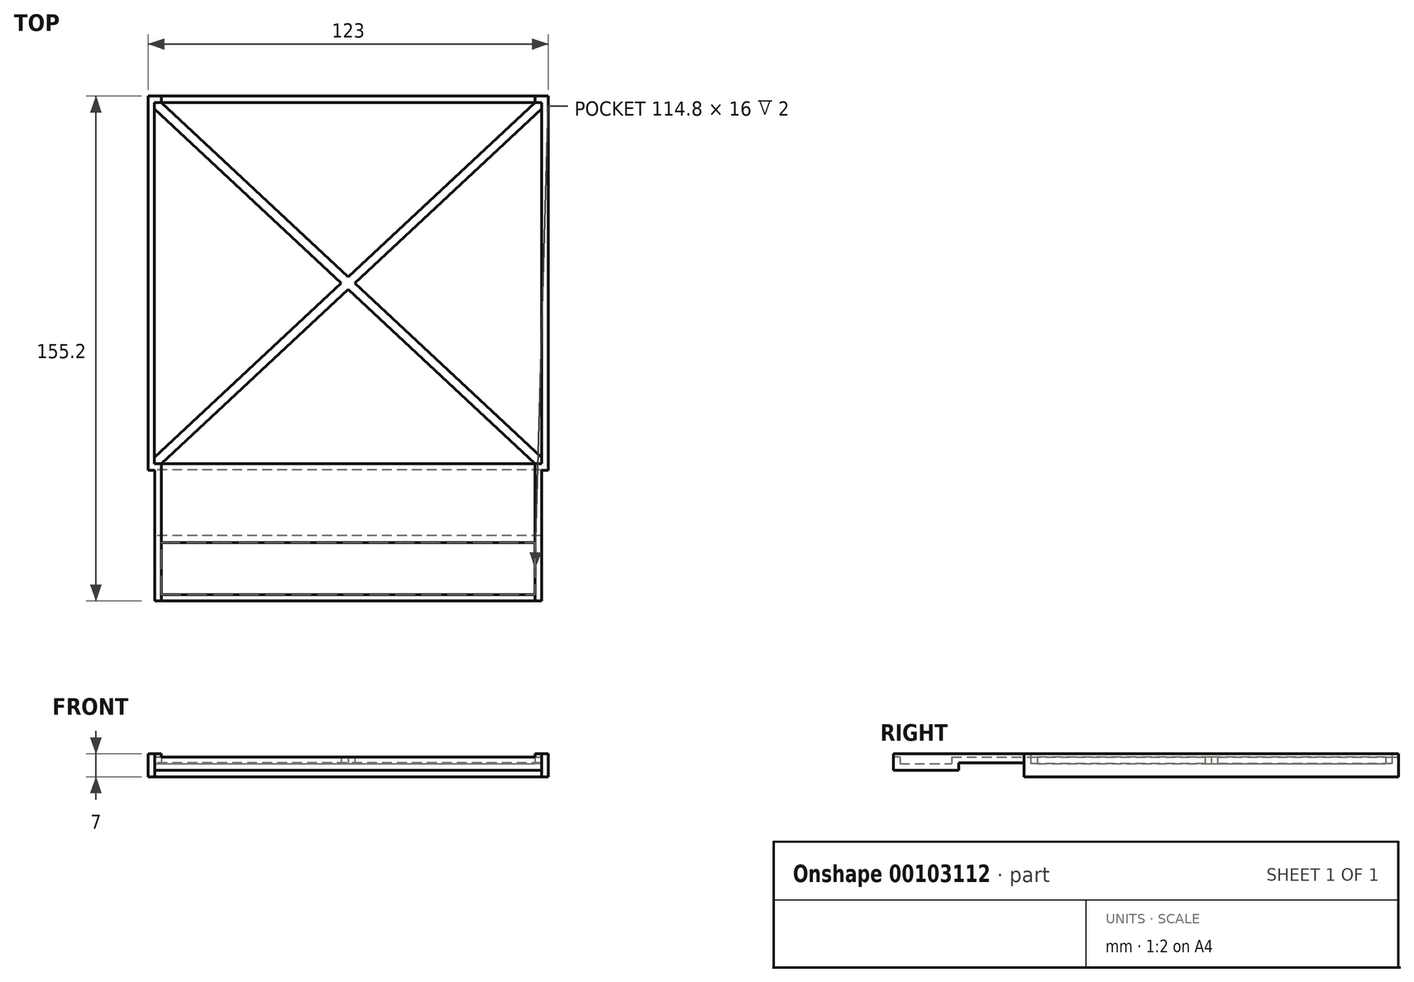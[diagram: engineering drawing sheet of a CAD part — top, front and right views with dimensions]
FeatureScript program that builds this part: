
annotation { "Feature Type Name" : "Feature", "Feature Type Description" : "" }
export const myFeature = defineFeature(function(context is Context, id is Id, definition is map)
    precondition{}
    {
        {
            var Q0;
            Q0=qCreatedBy(makeId("Top.planeOp"),FACE);
            var sketch = newSketch(context, id + "F0", { "sketchPlane" : qUnion([Q0])});
            skLineSegment(sketch, "E0.bottom", {"start": v(0, 0) * mm, "end": v(118.8, 0) * mm});
            skLineSegment(sketch, "E0.left", {"start": v(0, 0) * mm, "end": v(0, 40.2) * mm});
            skLineSegment(sketch, "E0.right", {"start": v(118.8, 0) * mm, "end": v(118.8, 40.2) * mm});
            skLineSegment(sketch, "E1.bottom", {"start": v(-2.1, 40.2) * mm, "end": v(0, 40.2) * mm});
            skLineSegment(sketch, "E1.top", {"start": v(-2.1, 155.2) * mm, "end": v(120.9, 155.2) * mm});
            skLineSegment(sketch, "E1.left", {"start": v(-2.1, 40.2) * mm, "end": v(-2.1, 155.2) * mm});
            skLineSegment(sketch, "E1.right", {"start": v(120.9, 40.2) * mm, "end": v(120.9, 155.2) * mm});
            skLineSegment(sketch, "E2.trimOffspring", {"start": v(118.8, 40.2) * mm, "end": v(120.9, 40.2) * mm});
            skSolve(sketch);
        }
        {
            var Q0;
            Q0=makeQuery(id+"F0.imprint","IMPRINT",FACE,{"disambiguationData":[TD([[makeQuery(id+"F0.imprint","IMPRINT",EDGE,{"derivedFrom":sQuery(id+"F0.wireOp",EDGE,"E0.bottom")}),1.0]])]});
            extrude(context, id + "F1", {"entities" : qUnion([Q0]), "depth" : 2 * mm});
        }
        {
            var Q0;
            Q0=makeQuery(id+"F1.opExtrude","CAP_FACE",FACE,{"disambiguationData":[OSD([sQuery(id+"F0.wireOp",EDGE,"E0.bottom"),sQuery(id+"F0.wireOp",EDGE,"E0.left"),sQuery(id+"F0.wireOp",EDGE,"E0.right"),sQuery(id+"F0.wireOp",EDGE,"E1.bottom"),sQuery(id+"F0.wireOp",EDGE,"E1.top"),sQuery(id+"F0.wireOp",EDGE,"E1.left"),sQuery(id+"F0.wireOp",EDGE,"E1.right"),sQuery(id+"F0.wireOp",EDGE,"E2.trimOffspring")])],"isStart":false});
            var sketch = newSketch(context, id + "F2", { "sketchPlane" : qUnion([Q0])});
            skLineSegment(sketch, "E3.0", {"start": v(-0.1, 42.2) * mm, "end": v(2, 42.2) * mm});
            skLineSegment(sketch, "E3.1", {"start": v(2, 2) * mm, "end": v(2, 42.2) * mm});
            skLineSegment(sketch, "E3.2", {"start": v(-0.1, 42.2) * mm, "end": v(-0.1, 153.2) * mm});
            skLineSegment(sketch, "E3.3", {"start": v(2, 2) * mm, "end": v(116.8, 2) * mm});
            skLineSegment(sketch, "E3.4", {"start": v(-0.1, 153.2) * mm, "end": v(118.9, 153.2) * mm});
            skLineSegment(sketch, "E3.5", {"start": v(118.9, 42.2) * mm, "end": v(118.9, 153.2) * mm});
            skLineSegment(sketch, "E3.6", {"start": v(116.8, 42.2) * mm, "end": v(118.9, 42.2) * mm});
            skLineSegment(sketch, "E3.7", {"start": v(116.8, 2) * mm, "end": v(116.8, 42.2) * mm});
            skSolve(sketch);
        }
        {
            var Q0;
            Q0=makeQuery(id+"F2.imprint","IMPRINT",FACE,{"disambiguationData":[TD([[makeQuery(id+"F2.imprint","IMPRINT",EDGE,{"derivedFrom":sQuery(id+"F2.wireOp",EDGE,"E3.0")}),-1.0]])]});
            extrude(context, id + "F3", {"entities" : qUnion([Q0]), "operationType" : NewBodyOperationType.ADD, "depth" : 3 * mm});
        }
        {
            var Q0;
            Q0=makeQuery(id+"F1.opExtrude","CAP_FACE",FACE,{"disambiguationData":[OSD([sQuery(id+"F0.wireOp",EDGE,"E0.bottom"),sQuery(id+"F0.wireOp",EDGE,"E0.left"),sQuery(id+"F0.wireOp",EDGE,"E0.right"),sQuery(id+"F0.wireOp",EDGE,"E1.bottom"),sQuery(id+"F0.wireOp",EDGE,"E1.top"),sQuery(id+"F0.wireOp",EDGE,"E1.left"),sQuery(id+"F0.wireOp",EDGE,"E1.right"),sQuery(id+"F0.wireOp",EDGE,"E2.trimOffspring")])],"isStart":false});
            var sketch = newSketch(context, id + "F4", { "sketchPlane" : qUnion([Q0])});
            skLineSegment(sketch, "E4.bottom", {"start": v(2, 42.2) * mm, "end": v(116.8, 42.2) * mm});
            skLineSegment(sketch, "E4.top", {"start": v(2, 18) * mm, "end": v(116.8, 18) * mm});
            skLineSegment(sketch, "E4.left", {"start": v(2, 42.2) * mm, "end": v(2, 18) * mm});
            skLineSegment(sketch, "E4.right", {"start": v(116.8, 42.2) * mm, "end": v(116.8, 18) * mm});
            skLineSegment(sketch, "E5", {"start": v(-0.1, 42.2) * mm, "end": v(118.9, 153.2) * mm});
            skLineSegment(sketch, "E6", {"start": v(-0.1, 153.2) * mm, "end": v(118.9, 42.2) * mm});
            skLineSegment(sketch, "E7", {"start": v(-0.1, 44.16) * mm, "end": v(57.3, 97.7) * mm});
            skLineSegment(sketch, "E8", {"start": v(57.3, 97.7) * mm, "end": v(-0.1, 151.24) * mm});
            skLineSegment(sketch, "E9", {"start": v(2, 42.2) * mm, "end": v(59.4, 95.74) * mm});
            skLineSegment(sketch, "E10", {"start": v(59.4, 95.74) * mm, "end": v(116.8, 42.2) * mm});
            skLineSegment(sketch, "E11", {"start": v(2, 153.2) * mm, "end": v(59.4, 99.66) * mm});
            skLineSegment(sketch, "E12", {"start": v(59.4, 99.66) * mm, "end": v(116.8, 153.2) * mm});
            skLineSegment(sketch, "E13", {"start": v(118.9, 151.24) * mm, "end": v(61.5, 97.7) * mm});
            skLineSegment(sketch, "E14", {"start": v(61.5, 97.7) * mm, "end": v(118.9, 44.16) * mm});
            skSolve(sketch);
        }
        {
            var Q0;
            Q0=makeQuery(id+"F4.imprint","IMPRINT",FACE,{"disambiguationData":[TD([[makeQuery(id+"F4.imprint","IMPRINT",EDGE,{"derivedFrom":sQuery(id+"F4.wireOp",EDGE,"E4.bottom")}),-1.0]])]});
            var Q1;
            Q1=makeQuery(id+"F4.imprint","IMPRINT",FACE,{"disambiguationData":[TD([[makeQuery(id+"F4.imprint","IMPRINT",EDGE,{"derivedFrom":sQuery(id+"F4.wireOp",EDGE,"E9")}),1.0]])]});
            var Q2;
            {var subQ1=sQuery(id+"F4.wireOp",EDGE,"E13");Q2=makeQuery(id+"F4.imprint","IMPRINT",FACE,{"disambiguationData":[TD([[makeQuery(id+"F4.imprint","IMPRINT",EDGE,{"derivedFrom":subQ1}),-1.0]])]});}
            var Q3;
            {var subQ1=sQuery(id+"F4.wireOp",EDGE,"E11");Q3=makeQuery(id+"F4.imprint","IMPRINT",FACE,{"disambiguationData":[TD([[makeQuery(id+"F4.imprint","IMPRINT",EDGE,{"derivedFrom":subQ1}),-1.0]])]});}
            var Q4;
            {var subQ1=sQuery(id+"F4.wireOp",EDGE,"E7");Q4=makeQuery(id+"F4.imprint","IMPRINT",FACE,{"disambiguationData":[TD([[makeQuery(id+"F4.imprint","IMPRINT",EDGE,{"derivedFrom":subQ1}),-1.0]])]});}
            extrude(context, id + "F5", {"entities" : qUnion([Q0, Q1, Q2, Q3, Q4]), "operationType" : NewBodyOperationType.ADD, "depth" : 2 * mm});
        }
        {
            var Q0;
            Q0=makeQuery(id+"F1.opExtrude","CAP_FACE",FACE,{"disambiguationData":[OSD([sQuery(id+"F0.wireOp",EDGE,"E0.bottom"),sQuery(id+"F0.wireOp",EDGE,"E0.left"),sQuery(id+"F0.wireOp",EDGE,"E0.right"),sQuery(id+"F0.wireOp",EDGE,"E1.bottom"),sQuery(id+"F0.wireOp",EDGE,"E1.top"),sQuery(id+"F0.wireOp",EDGE,"E1.left"),sQuery(id+"F0.wireOp",EDGE,"E1.right"),sQuery(id+"F0.wireOp",EDGE,"E2.trimOffspring")])],"isStart":true});
            var sketch = newSketch(context, id + "F6", { "sketchPlane" : qUnion([Q0])});
            skLineSegment(sketch, "E15.bottom", {"start": v(118.8, -40.3) * mm, "end": v(0, -40.3) * mm});
            skLineSegment(sketch, "E15.top", {"start": v(118.8, -20.1) * mm, "end": v(0, -20.1) * mm});
            skLineSegment(sketch, "E15.left", {"start": v(118.8, -40.3) * mm, "end": v(118.8, -20.1) * mm});
            skLineSegment(sketch, "E15.right", {"start": v(0, -40.3) * mm, "end": v(0, -20.1) * mm});
            skSolve(sketch);
        }
        {
            var Q0;
            {var subQ5=sQuery(id+"F6.wireOp",EDGE,"E15.bottom");Q0=makeQuery(id+"F6.imprint","IMPRINT",FACE,{"disambiguationData":[TD([[makeQuery(id+"F6.imprint","IMPRINT",EDGE,{"derivedFrom":subQ5}),-1.0]])]});}
            extrude(context, id + "F7", {"entities" : qUnion([Q0]), "operationType" : NewBodyOperationType.REMOVE, "oppositeDirection" : true, "depth" : 2.2 * mm});
        }
        {
            var Q0;
            Q0=makeQuery(id+"F3.opExtrude","CAP_FACE",FACE,{"disambiguationData":[OSD([sQuery(id+"F0.wireOp",EDGE,"E0.bottom"),sQuery(id+"F0.wireOp",EDGE,"E0.left"),sQuery(id+"F0.wireOp",EDGE,"E0.right"),sQuery(id+"F0.wireOp",EDGE,"E1.bottom"),sQuery(id+"F0.wireOp",EDGE,"E1.top"),sQuery(id+"F0.wireOp",EDGE,"E1.left"),sQuery(id+"F0.wireOp",EDGE,"E1.right"),sQuery(id+"F0.wireOp",EDGE,"E2.trimOffspring"),sQuery(id+"F2.wireOp",EDGE,"E3.0"),sQuery(id+"F2.wireOp",EDGE,"E3.1"),sQuery(id+"F2.wireOp",EDGE,"E3.2"),sQuery(id+"F2.wireOp",EDGE,"E3.3"),sQuery(id+"F2.wireOp",EDGE,"E3.4"),sQuery(id+"F2.wireOp",EDGE,"E3.5"),sQuery(id+"F2.wireOp",EDGE,"E3.6"),sQuery(id+"F2.wireOp",EDGE,"E3.7")])],"isStart":false});
            var sketch = newSketch(context, id + "F8", { "sketchPlane" : qUnion([Q0])});
            skLineSegment(sketch, "E16.bottom", {"start": v(2, 2) * mm, "end": v(116.8, 2) * mm});
            skLineSegment(sketch, "E16.top", {"start": v(2, 0) * mm, "end": v(116.8, 0) * mm});
            skLineSegment(sketch, "E16.left", {"start": v(2, 2) * mm, "end": v(2, 0) * mm});
            skLineSegment(sketch, "E16.right", {"start": v(116.8, 2) * mm, "end": v(116.8, 0) * mm});
            skSolve(sketch);
        }
        {
            var Q0;
            Q0=makeQuery(id+"F8.imprint","IMPRINT",FACE,{"disambiguationData":[TD([[makeQuery(id+"F8.imprint","IMPRINT",EDGE,{"derivedFrom":sQuery(id+"F8.wireOp",EDGE,"E16.bottom")}),-1.0]])]});
            extrude(context, id + "F9", {"entities" : qUnion([Q0]), "operationType" : NewBodyOperationType.REMOVE, "oppositeDirection" : true, "depth" : 1 * mm});
        }
        {
            var Q0;
            Q0=makeQuery(id+"F3.opExtrude","CAP_FACE",FACE,{"disambiguationData":[OSD([sQuery(id+"F0.wireOp",EDGE,"E0.bottom"),sQuery(id+"F0.wireOp",EDGE,"E0.left"),sQuery(id+"F0.wireOp",EDGE,"E0.right"),sQuery(id+"F0.wireOp",EDGE,"E1.bottom"),sQuery(id+"F0.wireOp",EDGE,"E1.top"),sQuery(id+"F0.wireOp",EDGE,"E1.left"),sQuery(id+"F0.wireOp",EDGE,"E1.right"),sQuery(id+"F0.wireOp",EDGE,"E2.trimOffspring"),sQuery(id+"F2.wireOp",EDGE,"E3.0"),sQuery(id+"F2.wireOp",EDGE,"E3.1"),sQuery(id+"F2.wireOp",EDGE,"E3.2"),sQuery(id+"F2.wireOp",EDGE,"E3.3"),sQuery(id+"F2.wireOp",EDGE,"E3.4"),sQuery(id+"F2.wireOp",EDGE,"E3.5"),sQuery(id+"F2.wireOp",EDGE,"E3.6"),sQuery(id+"F2.wireOp",EDGE,"E3.7")])],"isStart":false});
            var sketch = newSketch(context, id + "F10", { "sketchPlane" : qUnion([Q0])});
            skLineSegment(sketch, "E17.bottom", {"start": v(116.8, 153.2) * mm, "end": v(2, 153.2) * mm});
            skLineSegment(sketch, "E17.top", {"start": v(116.8, 155.2) * mm, "end": v(2, 155.2) * mm});
            skLineSegment(sketch, "E17.left", {"start": v(116.8, 153.2) * mm, "end": v(116.8, 155.2) * mm});
            skLineSegment(sketch, "E17.right", {"start": v(2, 153.2) * mm, "end": v(2, 155.2) * mm});
            skPoint(sketch, "E17.middle", {"position": v(59.4, 154.2) * mm});
            skPoint(sketch, "E17.middle.positionSnap0", {"position": v(59.4, 155.2) * mm});
            skPoint(sketch, "E17.centerSnap0", {"position": v(59.4, 155.2) * mm});
            skSolve(sketch);
        }
        {
            var Q0;
            Q0=makeQuery(id+"F10.imprint","IMPRINT",FACE,{"disambiguationData":[TD([[makeQuery(id+"F10.imprint","IMPRINT",EDGE,{"derivedFrom":sQuery(id+"F10.wireOp",EDGE,"E17.bottom")}),1.0]])]});
            extrude(context, id + "F11", {"entities" : qUnion([Q0]), "operationType" : NewBodyOperationType.REMOVE, "oppositeDirection" : true, "depth" : 1 * mm});
        }
        {
            var Q0;
            {var subQ0=sQuery(id+"F0.wireOp",EDGE,"E2.trimOffspring");var subQ1=sQuery(id+"F0.wireOp",EDGE,"E1.left");var subQ2=sQuery(id+"F0.wireOp",EDGE,"E1.bottom");var subQ3=sQuery(id+"F0.wireOp",EDGE,"E1.top");var subQ4=sQuery(id+"F0.wireOp",EDGE,"E1.right");Q0=makeQuery(id+"F7.boolean.opBoolean","SPLIT",FACE,{"disambiguationData":[TD([makeQuery(id+"F1.opExtrude","SWEPT_FACE",FACE,{"disambiguationData":[OSD([subQ2])]})])],"derivedFrom":makeQuery(id+"F1.opExtrude","CAP_FACE",FACE,{"disambiguationData":[OSD([sQuery(id+"F0.wireOp",EDGE,"E0.bottom"),sQuery(id+"F0.wireOp",EDGE,"E0.left"),sQuery(id+"F0.wireOp",EDGE,"E0.right"),subQ2,subQ3,subQ1,subQ4,subQ0])],"isStart":true})});}
            extrude(context, id + "F12", {"entities" : qUnion([Q0]), "operationType" : NewBodyOperationType.ADD, "depth" : 2 * mm});
        }
    });
